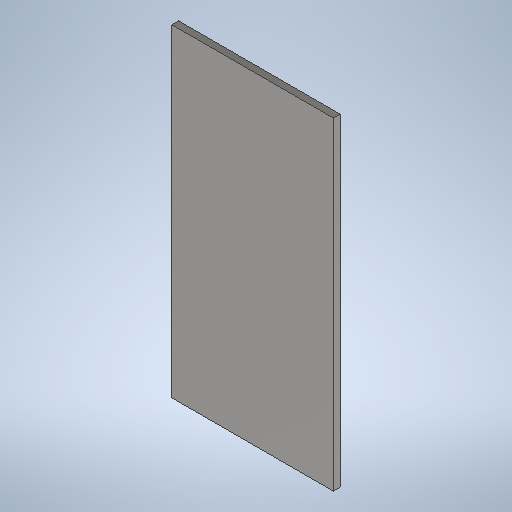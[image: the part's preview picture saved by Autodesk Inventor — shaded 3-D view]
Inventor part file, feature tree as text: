
AUTODESK INVENTOR PART (.ipt)
format: ipt  version: 2025 (Build 290162010, 162A)  size: 222,720 bytes
history: native  units: in
note: dims shown in document units (in); Inventor stores cm internally (conversion verified against a paired STEP export)
features: extrude x1, sketch x1
ambient origin geometry x8: Origin, YZ Plane, XZ Plane, XY Plane, X Axis, Y Axis, Z Axis, Center Point
bodies: Solid1 (feature_tree)
feature tree (2):
  extrude  "Extrusion1"  Depth=3.0in
  sketch  "Sketch1"  dims[d1=6.0in d2=3.0in d3=0.125in d4=0.0in]
